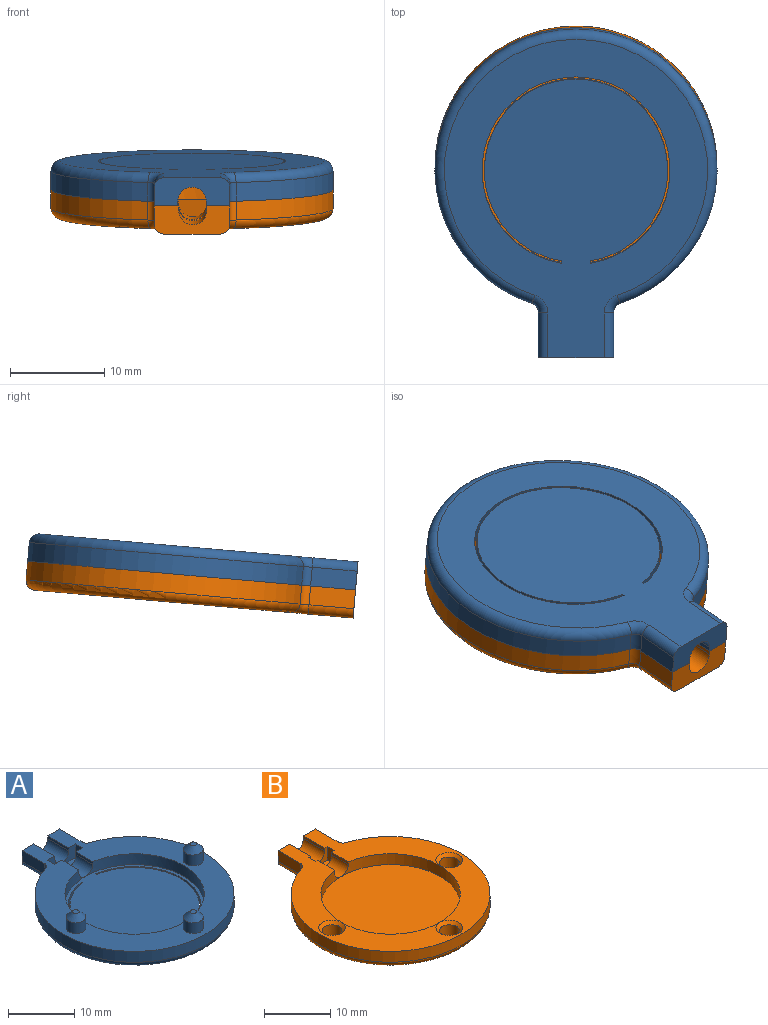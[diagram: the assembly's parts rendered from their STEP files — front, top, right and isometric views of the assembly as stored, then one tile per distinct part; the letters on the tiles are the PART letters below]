
ASSEMBLY  parts=2 mates=1
PART A: 39 faces, bbox 32.5x36.2x6 mm
  f0: plane 4.5x0.5mm, normal (-1,0,0), area 2.3mm2, adj f2,f5,f6,f37
  f1: plane 4.5x0.5mm, normal (1,0,0), area 2.3mm2, adj f2,f5,f6,f37
  f2: cylinder r=1.5mm len=4.5mm, axis (0,1,0), area 21.2mm2, adj f0,f1,f5,f37
  f3: plane 34x28mm, normal (0,0,-1), area 638.5mm2, adj f5,f22,f25,f26,f27,f28,f29,f30
  f4: plane 21x21mm, normal (0,0,1), area 331.6mm2, adj f12,f29,f30,f31,f32
  f5: plane 8x3mm, normal (0,1,0), area 18.5mm2, adj f0,f1,f2,f3,f6,f7,f9,f22
  f6: plane 35x30mm, normal (0,0,1), area 347.8mm2, adj f0,f1,f5,f7,f8,f9,f10,f11
  f7: plane 4.8x2mm, normal (-1,0,0), area 9.6mm2, adj f5,f6,f22,f23
  f8: cylinder r=15mm len=30mm, axis (0,0,-1), area 169.4mm2, adj f6,f23,f24,f28
  f9: plane 4.8x2mm, normal (1,0,0), area 9.6mm2, adj f5,f6,f24,f25
  f10: plane 3.61x0.5mm, normal (-1,0,0), area 1.8mm2, adj f6,f12,f33,f35
  f11: plane 3.61x0.5mm, normal (1,0,0), area 1.8mm2, adj f6,f12,f33,f35
  f12: cylinder r=10.5mm len=21mm, axis (0,0,1), area 126.9mm2, adj f4,f6,f10,f11,f33
  f13: cylinder r=1.5mm len=3mm, axis (0,0,-1), area 18.8mm2, adj f6,f19
  f14: plane 1x1mm, normal (0,0,1), area 0.8mm2, adj f19
  f15: cylinder r=1.5mm len=3mm, axis (0,0,-1), area 18.8mm2, adj f6,f21
  f16: plane 1x1mm, normal (0,0,1), area 0.8mm2, adj f21
  f17: cylinder r=1.5mm len=3mm, axis (0,0,-1), area 18.8mm2, adj f6,f20
  f18: plane 1x1mm, normal (0,0,1), area 0.8mm2, adj f20
  f19: cone r=0.5mm half-angle=45deg, axis (0,0,-1), area 8.9mm2, adj f13,f14
  f20: cone r=0.5mm half-angle=45deg, axis (0,0,-1), area 8.9mm2, adj f17,f18
  f21: cone r=0.5mm half-angle=45deg, axis (0,0,-1), area 8.9mm2, adj f15,f16
  f22: cylinder r=1mm len=4.8mm, axis (0,-1,0), area 7.5mm2, adj f3,f5,f7,f26
  f23: cylinder r=1mm len=2mm, axis (0,0,-1), area 2.5mm2, adj f6,f7,f8,f26
  f24: cylinder r=1mm len=2mm, axis (0,0,-1), area 2.5mm2, adj f6,f8,f9,f27
  f25: cylinder r=1mm len=4.8mm, axis (0,1,0), area 7.5mm2, adj f3,f5,f9,f27
  f26: torus R=2mm, axis (0,0,1), area 2.7mm2, adj f3,f22,f23,f28
  f27: torus R=2mm, axis (0,0,1), area 2.7mm2, adj f3,f24,f25,f28
  f28: torus R=14mm, axis (0,0,1), area 129.8mm2, adj f3,f8,f26,f27
  f29: cylinder r=9.75mm len=19.5mm, axis (0,0,1), area 58.2mm2, adj f3,f4,f30,f32
  f30: plane 1x0.25mm, normal (-1,0,0), area 0.3mm2, adj f3,f4,f29,f31
  f31: cylinder r=10mm len=20mm, axis (0,0,1), area 59.8mm2, adj f3,f4,f30,f32
  f32: plane 1x0.25mm, normal (1,0,0), area 0.3mm2, adj f3,f4,f29,f31
  f33: cylinder r=1.5mm len=3.61mm, axis (0,1,0), area 16.7mm2, adj f10,f11,f12,f35
  f34: plane 2.5x1.5mm, normal (1,0,0), area 3.7mm2, adj f6,f35,f37,f38
  f35: plane 6x2.5mm, normal (0,1,0), area 10mm2, adj f6,f10,f11,f33,f34,f36,f38
  f36: plane 2.5x1.5mm, normal (-1,0,0), area 3.7mm2, adj f6,f35,f37,f38
  f37: plane 6x2.5mm, normal (0,-1,0), area 10mm2, adj f0,f1,f2,f6,f34,f36,f38
  f38: plane 6x1.5mm, normal (0,0,1), area 9mm2, adj f34,f35,f36,f37
PART B: 32 faces, bbox 32.5x36.2x3 mm
  f0: plane 35x30mm, normal (0,0,1), area 334.3mm2, adj f1,f2,f4,f5,f6,f7,f9,f10
  f1: plane 4.5x0.5mm, normal (-1,0,0), area 2.3mm2, adj f0,f3,f4,f27
  f2: plane 4.5x0.5mm, normal (1,0,0), area 2.3mm2, adj f0,f3,f4,f27
  f3: cylinder r=1.5mm len=4.5mm, axis (0,1,0), area 21.2mm2, adj f1,f2,f4,f27
  f4: plane 8x3mm, normal (0,1,0), area 18.5mm2, adj f0,f1,f2,f3,f5,f7,f8,f19
  f5: plane 4.8x2mm, normal (-1,0,0), area 9.6mm2, adj f0,f4,f19,f20
  f6: cylinder r=15mm len=30mm, axis (0,0,-1), area 169.4mm2, adj f0,f20,f21,f25
  f7: plane 4.8x2mm, normal (1,0,0), area 9.6mm2, adj f0,f4,f21,f22
  f8: plane 34x28mm, normal (0,0,-1), area 632mm2, adj f4,f13,f14,f15,f19,f22,f23,f24
  f9: plane 3.6x0.5mm, normal (-1,0,0), area 1.8mm2, adj f0,f11,f26,f29
  f10: plane 3.62x0.5mm, normal (1,0,0), area 1.8mm2, adj f0,f11,f26,f29
  f11: cylinder r=10.5mm len=21mm, axis (0,0,1), area 126.9mm2, adj f0,f9,f10,f12,f26
  f12: plane 21x21mm, normal (0,0,1), area 346.4mm2, adj f11
  f13: cylinder r=1.5mm len=3mm, axis (0,0,1), area 23.6mm2, adj f8,f16
  f14: cylinder r=1.5mm len=3mm, axis (0,0,1), area 23.6mm2, adj f8,f18
  f15: cylinder r=1.5mm len=3mm, axis (0,0,1), area 23.6mm2, adj f8,f17
  f16: cone r=1.5mm half-angle=45deg, axis (0,0,1), area 7.8mm2, adj f0,f13
  f17: cone r=1.5mm half-angle=45deg, axis (0,0,1), area 7.8mm2, adj f0,f15
  f18: cone r=1.5mm half-angle=45deg, axis (0,0,1), area 7.8mm2, adj f0,f14
  f19: cylinder r=1mm len=4.8mm, axis (0,-1,0), area 7.5mm2, adj f4,f5,f8,f23
  f20: cylinder r=1mm len=2mm, axis (0,0,-1), area 2.5mm2, adj f0,f5,f6,f23
  f21: cylinder r=1mm len=2mm, axis (0,0,-1), area 2.5mm2, adj f0,f6,f7,f24
  f22: cylinder r=1mm len=4.8mm, axis (0,1,0), area 7.5mm2, adj f4,f7,f8,f24
  f23: torus R=2mm, axis (0,0,1), area 2.7mm2, adj f8,f19,f20,f25
  f24: torus R=2mm, axis (0,0,1), area 2.7mm2, adj f8,f21,f22,f25
  f25: torus R=14mm, axis (0,0,1), area 129.8mm2, adj f6,f8,f23,f24
  f26: cylinder r=1.5mm len=3.62mm, axis (0,1,0), area 16.7mm2, adj f9,f10,f11,f29
  f27: plane 4x2.5mm, normal (0,-1,0), area 5mm2, adj f0,f1,f2,f3,f28,f30,f31
  f28: plane 2.5x1.5mm, normal (1,0,0), area 3.7mm2, adj f0,f27,f29,f31
  f29: plane 4x2.5mm, normal (0,1,0), area 5mm2, adj f0,f9,f10,f26,f28,f30,f31
  f30: plane 2.5x1.5mm, normal (-1,0,0), area 3.7mm2, adj f0,f27,f29,f31
  f31: plane 4x1.5mm, normal (0,0,1), area 6mm2, adj f27,f28,f29,f30
PLACE A rot(axis=(-1,0,0),175deg) t=(-7.16,5.85,7.43)mm
PLACE B rot(axis=(0,-0.04,1),180deg) t=(-7.16,6.37,1.45)mm
MATE revolute A.f8 <-> B.f6  axis (0,0.09,-1) through (-7.16,6.11,4.44)mm
